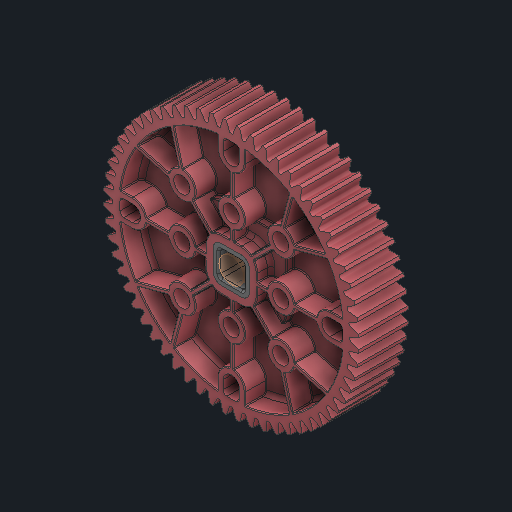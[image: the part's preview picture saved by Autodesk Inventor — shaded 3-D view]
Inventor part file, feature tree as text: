
AUTODESK INVENTOR PART (.ipt)
format: ipt  version: 2024 (Build 280153000, 153)  size: 5,419,008 bytes
history: native  units: in
note: dims shown in document units (in); Inventor stores cm internally (conversion verified against a paired STEP export)
features: other x6, sketch x1
ambient origin geometry x8: Origin, YZ Plane, XZ Plane, XY Plane, X Axis, Y Axis, Z Axis, Center Point
bodies: Solid1 (feature_tree), Solid2 (feature_tree)
feature tree (7):
  other  "HS 60T Gear, No Insert.ipt"
  other  "Solid1::HS 60T Gear, No Insert.ipt"
  other  "Solid2::HS 60T Gear, No Insert.ipt"
  other  "TaggingFeature1"
  sketch  "Sketch1"  dims[d0=0.3937in]
  other  "Srf1"
  other  "Srf1::Derived"
